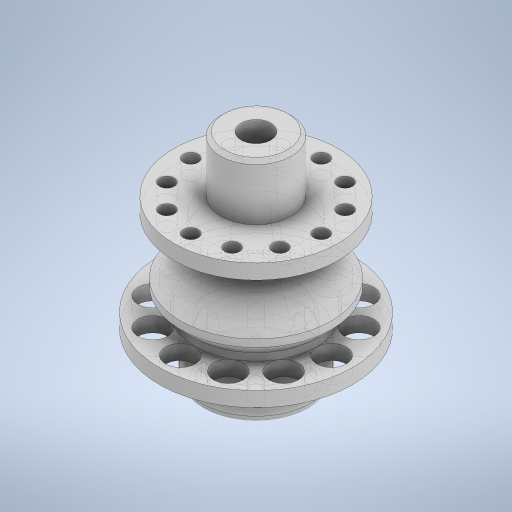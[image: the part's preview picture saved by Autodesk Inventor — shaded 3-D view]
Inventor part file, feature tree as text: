
AUTODESK INVENTOR PART (.ipt)
format: ipt  version: 2023.2 (Build 272271000, 271)  size: 719,872 bytes
history: native  units: mm
features: extrude x6, sketch x5, pattern_circular x3, fillet x3, other x2, revolve x2, chamfer x1
ambient origin geometry x8: Origin, YZ Plane, XZ Plane, XY Plane, X Axis, Y Axis, Z Axis, Center Point
bodies: Body1 (feature_tree)
feature tree (22):
  other  "Твердое тело1"
  extrude  "Выдавливание1"  Depth=14.7mm
  extrude  "Выдавливание2"  Depth=2.0mm TaperAngle=0.0deg
  other  "РабПлоскость1"
  extrude  "Выдавливание3"  Depth=12.0mm
  pattern_circular  "Круговой массив1"  [2 undecoded]
  extrude  "Выдавливание4"  Depth=7.35mm
  extrude  "Выдавливание5"  Depth=2.0mm
  pattern_circular  "Круговой массив2"  [2 undecoded]
  revolve  "Вращение1"
  extrude  "Выдавливание6"  Depth=3.0mm TaperAngle=0.0deg
  pattern_circular  "Круговой массив3"  Count=8 Angle=360.0deg
  revolve  "Вращение2"
  chamfer  "Фаска2"  Distance=26.0mm
  fillet  "Сопряжение1"  Radius=2.0mm
  fillet  "Сопряжение2"  Radius=4.0mm
  fillet  "Сопряжение3"  Radius=2.0mm
  sketch  "Эскиз1"
  sketch  "Эскиз2"
  sketch  "Эскиз3"
  sketch  "Эскиз4"
  sketch  "Эскиз9"
note: 4 required parameter values undecoded (feature->parameter linkage not recoverable at this tier; creation-order binding heuristic only, values carry confidence <= 0.55)
